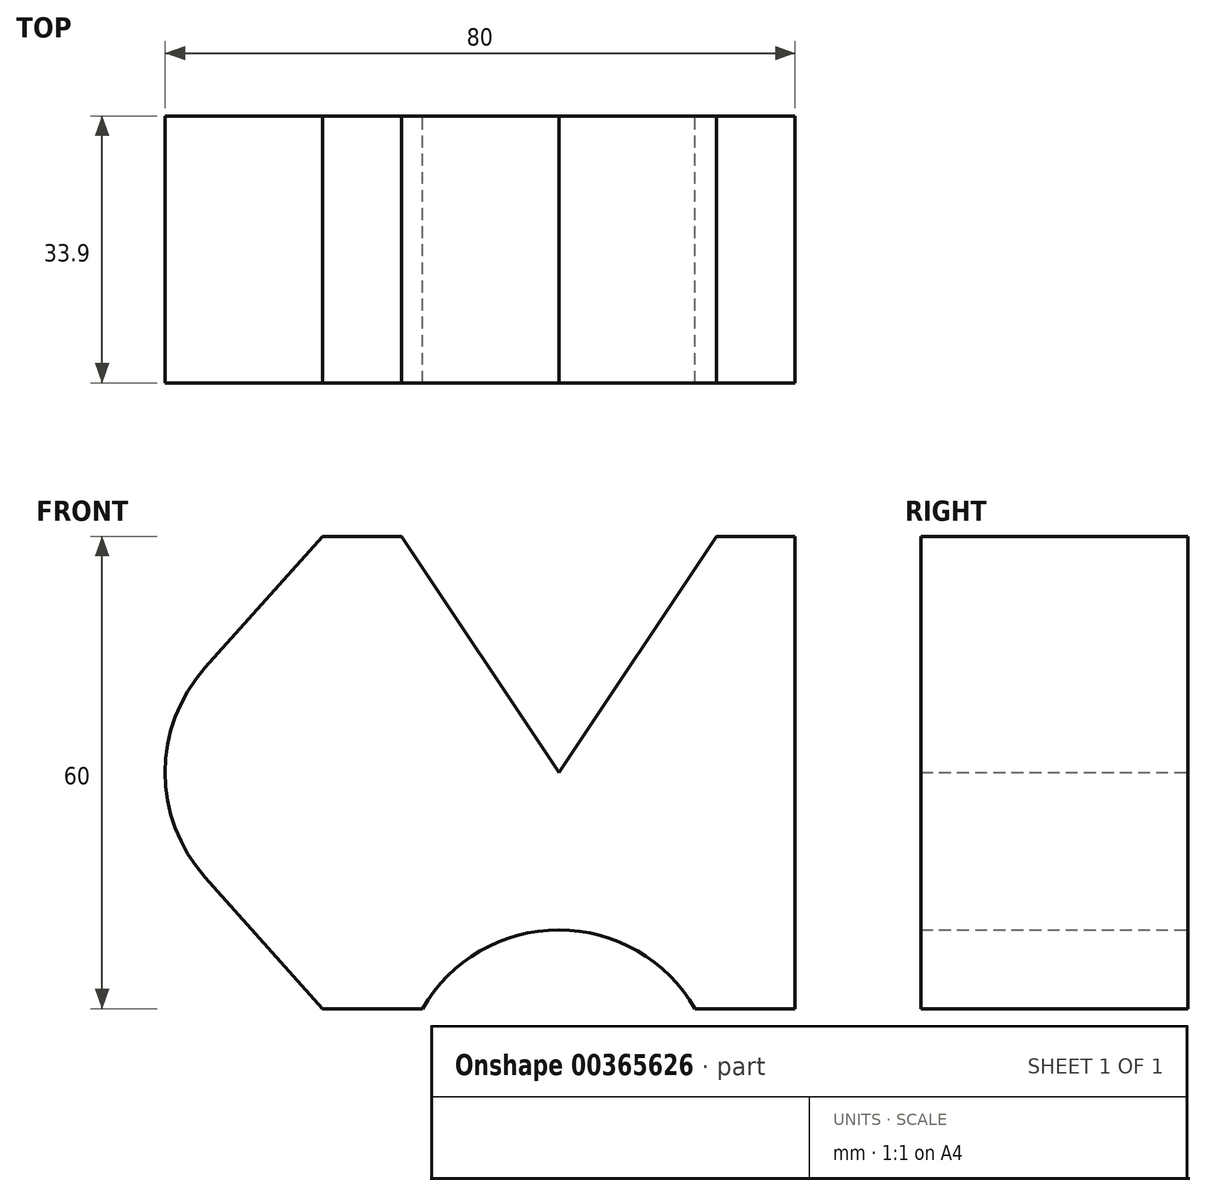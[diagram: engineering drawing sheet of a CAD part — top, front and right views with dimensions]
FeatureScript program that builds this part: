
annotation { "Feature Type Name" : "Feature", "Feature Type Description" : "" }
export const myFeature = defineFeature(function(context is Context, id is Id, definition is map)
    precondition{}
    {
        {
            var Q0;
            Q0=qCreatedBy(makeId("Front.planeOp"),FACE);
            var sketch = newSketch(context, id + "F0", { "sketchPlane" : qUnion([Q0])});
            skLineSegment(sketch, "E0", {"start": v(0, 0) * mm, "end": v(20, 30) * mm});
            skLineSegment(sketch, "E1", {"start": v(20, 30) * mm, "end": v(30, 30) * mm});
            skLineSegment(sketch, "E2", {"start": v(30, 30) * mm, "end": v(30, -30) * mm});
            skLineSegment(sketch, "E3", {"start": v(30, -30) * mm, "end": v(17.32, -30) * mm});
            skLineSegment(sketch, "E4", {"start": v(0, 0) * mm, "end": v(-20, 30) * mm});
            skLineSegment(sketch, "E5", {"start": v(-20, 30) * mm, "end": v(-30, 30) * mm});
            skLineSegment(sketch, "E6", {"start": v(-17.32, -30) * mm, "end": v(-30, -30) * mm});
            skLineSegment(sketch, "E7", {"start": v(-30, -30) * mm, "end": v(-44.9, -13.33) * mm});
            skLineSegment(sketch, "E8", {"start": v(-30, 30) * mm, "end": v(-44.9, 13.33) * mm});
            skArc(sketch, "E9", {"start": v(-44.9, 13.33) * mm, "mid": v(-50, 0) * mm, "end": v(-44.9, -13.33) * mm});
            skLineSegment(sketch, "E10", {"start": v(-30, 30) * mm, "end": v(-30, -47.23) * mm, "construction": true});
            skArc(sketch, "E11", {"start": v(17.32, -30) * mm, "mid": v(0, -20) * mm, "end": v(-17.32, -30) * mm});
            skSolve(sketch);
        }
        {
            var Q0;
            Q0=makeQuery(id+"F0.imprint","IMPRINT",FACE,{"disambiguationData":[TD([[makeQuery(id+"F0.imprint","IMPRINT",EDGE,{"derivedFrom":sQuery(id+"F0.wireOp",EDGE,"E0")}),-1.0]])]});
            extrude(context, id + "F1", {"entities" : qUnion([Q0]), "depth" : 33.9 * mm});
        }
    });
